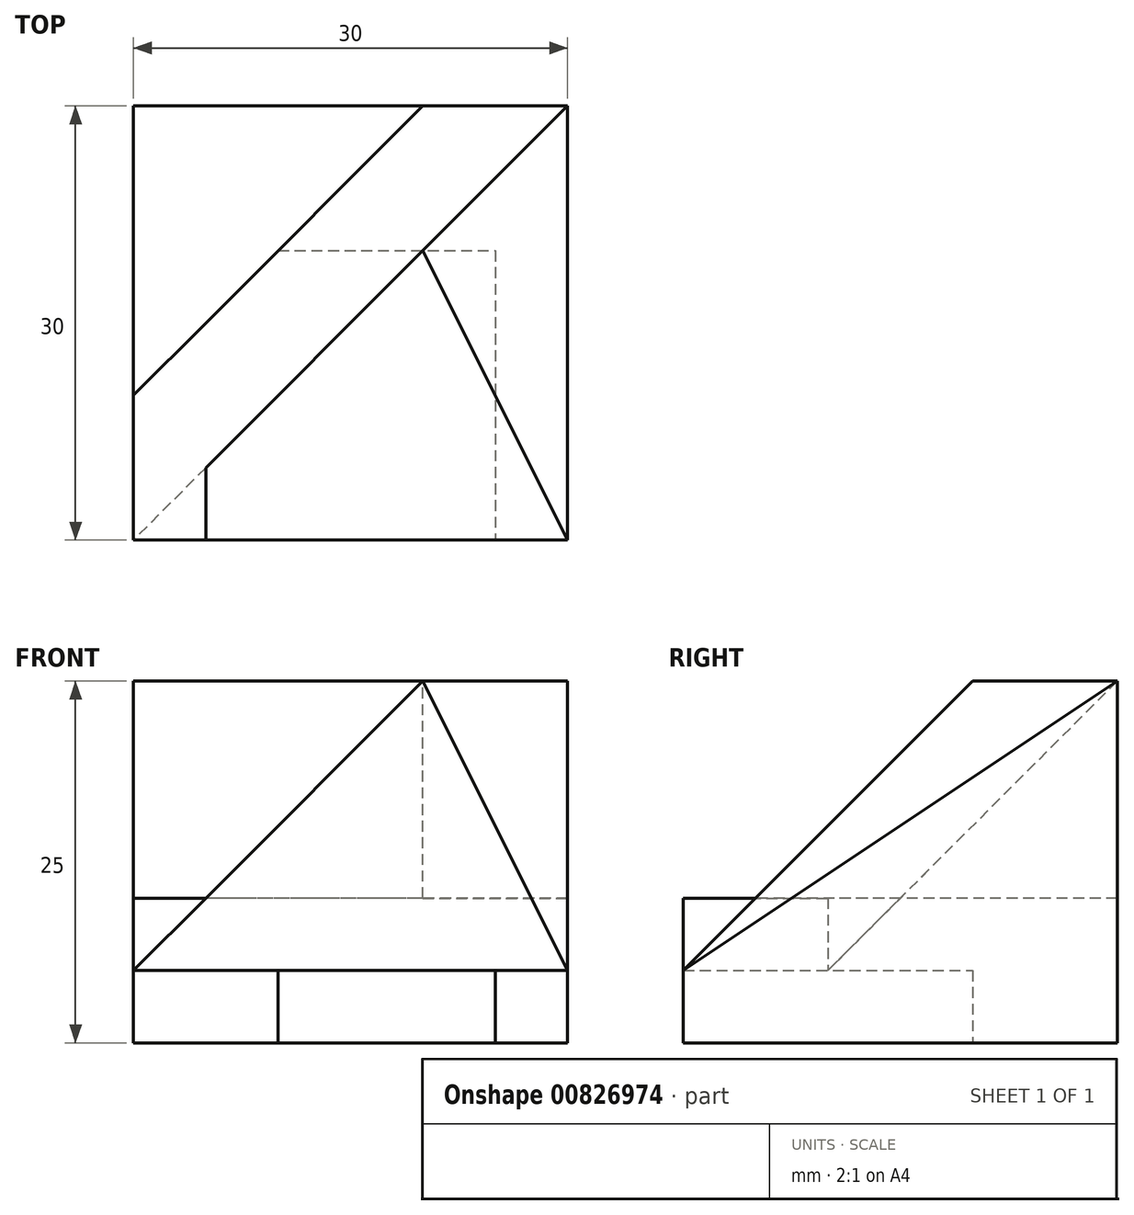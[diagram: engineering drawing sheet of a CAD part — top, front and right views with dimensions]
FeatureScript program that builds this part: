
annotation { "Feature Type Name" : "Feature", "Feature Type Description" : "" }
export const myFeature = defineFeature(function(context is Context, id is Id, definition is map)
    precondition{}
    {
        {
            var Q0;
            Q0=qCreatedBy(makeId("Top.planeOp"),FACE);
            var sketch = newSketch(context, id + "F0", { "sketchPlane" : qUnion([Q0])});
            skLineSegment(sketch, "E0.bottom", {"start": v(0, 0) * mm, "end": v(30, 0) * mm});
            skLineSegment(sketch, "E0.top", {"start": v(0, 30) * mm, "end": v(30, 30) * mm});
            skLineSegment(sketch, "E0.left", {"start": v(0, 0) * mm, "end": v(0, 30) * mm});
            skLineSegment(sketch, "E0.right", {"start": v(30, 0) * mm, "end": v(30, 30) * mm});
            skSolve(sketch);
        }
        {
            var Q0;
            Q0=makeQuery(id+"F0.imprint","IMPRINT",FACE,{"disambiguationData":[TD([[makeQuery(id+"F0.imprint","IMPRINT",EDGE,{"derivedFrom":sQuery(id+"F0.wireOp",EDGE,"E0.bottom")}),1.0]])]});
            extrude(context, id + "F1", {"entities" : qUnion([Q0]), "depth" : 25 * mm, "offsetDistance" : 25 * mm});
        }
        {
            var Q0;
            Q0=makeQuery(id+"F1.opExtrude","CAP_FACE",FACE,{"disambiguationData":[OSD([sQuery(id+"F0.wireOp",EDGE,"E0.bottom"),sQuery(id+"F0.wireOp",EDGE,"E0.top"),sQuery(id+"F0.wireOp",EDGE,"E0.left"),sQuery(id+"F0.wireOp",EDGE,"E0.right")])],"isStart":false});
            var sketch = newSketch(context, id + "F2", { "sketchPlane" : qUnion([Q0])});
            skLineSegment(sketch, "E1", {"start": v(20, 30) * mm, "end": v(0, 10) * mm});
            skLineSegment(sketch, "E2", {"start": v(30, 30) * mm, "end": v(0, 0) * mm});
            skLineSegment(sketch, "E3", {"start": v(30, 0) * mm, "end": v(20, 20) * mm});
            skSolve(sketch);
        }
        {
            var Q0;
            Q0=makeQuery(id+"F1.opExtrude","SWEPT_FACE",FACE,{"disambiguationData":[OSD([sQuery(id+"F0.wireOp",EDGE,"E0.bottom")])]});
            var sketch = newSketch(context, id + "F3", { "sketchPlane" : qUnion([Q0])});
            skLineSegment(sketch, "E4", {"start": v(0, 5) * mm, "end": v(30, 5) * mm});
            skLineSegment(sketch, "E5", {"start": v(0, 5) * mm, "end": v(20, 25) * mm});
            skLineSegment(sketch, "E6", {"start": v(20, 25) * mm, "end": v(30, 5) * mm});
            skLineSegment(sketch, "E7", {"start": v(10, 5) * mm, "end": v(10, 0) * mm});
            skLineSegment(sketch, "E8", {"start": v(25, 5) * mm, "end": v(25, 0) * mm});
            skLineSegment(sketch, "E9", {"start": v(0, 10) * mm, "end": v(5, 10) * mm, "construction": true});
            skSolve(sketch);
        }
        {
            var Q0;
            Q0=makeQuery(id+"F1.opExtrude","SWEPT_FACE",FACE,{"disambiguationData":[OSD([sQuery(id+"F0.wireOp",EDGE,"E0.right")])]});
            var sketch = newSketch(context, id + "F4", { "sketchPlane" : qUnion([Q0])});
            skLineSegment(sketch, "E10", {"start": v(0, 5) * mm, "end": v(30, 25) * mm});
            skLineSegment(sketch, "E11", {"start": v(0, 5) * mm, "end": v(20, 25) * mm});
            skLineSegment(sketch, "E12", {"start": v(20, 25) * mm, "end": v(0, 25) * mm});
            skLineSegment(sketch, "E13", {"start": v(0, 25) * mm, "end": v(0, 5) * mm});
            skSolve(sketch);
        }
        {
            var Q0;
            Q0=makeQuery(id+"F1.opExtrude","SWEPT_FACE",FACE,{"disambiguationData":[OSD([sQuery(id+"F0.wireOp",EDGE,"E0.left")])]});
            var sketch = newSketch(context, id + "F5", { "sketchPlane" : qUnion([Q0])});
            skLineSegment(sketch, "E14", {"start": v(-30, 25) * mm, "end": v(-10, 5) * mm});
            skLineSegment(sketch, "E15", {"start": v(0, 10) * mm, "end": v(-30, 10) * mm});
            skLineSegment(sketch, "E16", {"start": v(-10, 5) * mm, "end": v(-10, 10) * mm});
            skSolve(sketch);
        }
        {
            var Q0;
            Q0=makeQuery(id+"F1.opExtrude","CAP_FACE",FACE,{"disambiguationData":[OSD([sQuery(id+"F0.wireOp",EDGE,"E0.bottom"),sQuery(id+"F0.wireOp",EDGE,"E0.top"),sQuery(id+"F0.wireOp",EDGE,"E0.left"),sQuery(id+"F0.wireOp",EDGE,"E0.right")])],"isStart":true});
            var sketch = newSketch(context, id + "F6", { "sketchPlane" : qUnion([Q0])});
            skLineSegment(sketch, "E17", {"start": v(10, 0) * mm, "end": v(10, -20) * mm});
            skLineSegment(sketch, "E18", {"start": v(10, -20) * mm, "end": v(25, -20) * mm});
            skLineSegment(sketch, "E19", {"start": v(25, -20) * mm, "end": v(25, 0) * mm});
            skSolve(sketch);
        }
        {
            var Q1;
            {var subQ0=sQuery(id+"F2.wireOp",EDGE,"E1");Q1=makeQuery(id+"F2.imprint","IMPRINT",FACE,{"disambiguationData":[TD([[makeQuery(id+"F2.imprint","IMPRINT",EDGE,{"derivedFrom":subQ0}),-1.0]])]});}
            var Q2;
            Q2=sQuery(id+"F5.wireOp",VERTEX,"E14.end");
            loft(context, id + "F7", {"operationType" : NewBodyOperationType.REMOVE, "sheetProfilesArray" : [{ "sheetProfileEntities" : qUnion([Q1]) }, { "sheetProfileEntities" : qUnion([Q2]) }]});
        }
        {
            var Q1;
            {var subQ2=sQuery(id+"F2.wireOp",EDGE,"E3");Q1=makeQuery(id+"F2.imprint","IMPRINT",FACE,{"disambiguationData":[TD([[makeQuery(id+"F2.imprint","IMPRINT",EDGE,{"derivedFrom":subQ2}),-1.0]])]});}
            var Q2;
            Q2=sQuery(id+"F3.wireOp",VERTEX,"E4.end");
            loft(context, id + "F8", {"operationType" : NewBodyOperationType.REMOVE, "sheetProfilesArray" : [{ "sheetProfileEntities" : qUnion([Q1]) }, { "sheetProfileEntities" : qUnion([Q2]) }]});
        }
        {
            var Q1;
            {var subQ0=sQuery(id+"F3.wireOp",EDGE,"E6");Q1=makeQuery(id+"F3.imprint","IMPRINT",FACE,{"disambiguationData":[TD([[makeQuery(id+"F3.imprint","IMPRINT",EDGE,{"derivedFrom":subQ0}),1.0]])]});}
            var Q2;
            Q2=sQuery(id+"F2.wireOp",VERTEX,"E3.end");
            loft(context, id + "F9", {"operationType" : NewBodyOperationType.REMOVE, "sheetProfilesArray" : [{ "sheetProfileEntities" : qUnion([Q1]) }, { "sheetProfileEntities" : qUnion([Q2]) }]});
        }
        {
            var Q0;
            {var subQ0=sQuery(id+"F6.wireOp",EDGE,"E17");Q0=makeQuery(id+"F6.imprint","IMPRINT",FACE,{"disambiguationData":[TD([[makeQuery(id+"F6.imprint","IMPRINT",EDGE,{"derivedFrom":subQ0}),1.0]])]});}
            extrude(context, id + "F10", {"entities" : qUnion([Q0]), "operationType" : NewBodyOperationType.REMOVE, "oppositeDirection" : true, "depth" : 5 * mm, "offsetDistance" : 25 * mm});
        }
        {
            var Q0;
            Q0=makeQuery(id+"F4.imprint","IMPRINT",FACE,{"disambiguationData":[TD([[makeQuery(id+"F4.imprint","IMPRINT",EDGE,{"derivedFrom":sQuery(id+"F4.wireOp",EDGE,"E11")}),1.0]])]});
            extrude(context, id + "F11", {"entities" : qUnion([Q0]), "operationType" : NewBodyOperationType.REMOVE, "endBound" : BoundingType.THROUGH_ALL, "oppositeDirection" : true, "depth" : 25 * mm, "offsetDistance" : 25 * mm});
        }
        {
            var Q0;
            {var subQ3=sQuery(id+"F2.wireOp",EDGE,"E1");Q0=makeQuery(id+"F2.imprint","IMPRINT",FACE,{"disambiguationData":[TD([[makeQuery(id+"F2.imprint","IMPRINT",EDGE,{"derivedFrom":subQ3}),1.0]])]});}
            extrude(context, id + "F12", {"entities" : qUnion([Q0]), "operationType" : NewBodyOperationType.REMOVE, "oppositeDirection" : true, "depth" : 15 * mm, "offsetDistance" : 25 * mm});
        }
        {
            var Q0;
            {var subQ1=sQuery(id+"F0.wireOp",EDGE,"E0.bottom");var subQ2=sQuery(id+"F0.wireOp",EDGE,"E0.left");Q0=makeQuery(id+"F11.boolean.opBoolean","SPLIT",FACE,{"disambiguationData":[TD([makeQuery(id+"F1.opExtrude","SWEPT_FACE",FACE,{"disambiguationData":[OSD([subQ2])]})])],"derivedFrom":makeQuery(id+"F1.opExtrude","SWEPT_FACE",FACE,{"disambiguationData":[OSD([subQ1])]})});}
            var sketch = newSketch(context, id + "F13", { "sketchPlane" : qUnion([Q0])});
            skLineSegment(sketch, "E20", {"start": v(5, 10) * mm, "end": v(0, 5) * mm});
            skLineSegment(sketch, "E21", {"start": v(0, 5) * mm, "end": v(0, 10) * mm});
            skLineSegment(sketch, "E22", {"start": v(0, 10) * mm, "end": v(5, 10) * mm});
            skSolve(sketch);
        }
        {
            var Q0;
            Q0=makeQuery(id+"F13.imprint","IMPRINT",FACE,{"disambiguationData":[TD([[makeQuery(id+"F13.imprint","IMPRINT",EDGE,{"derivedFrom":sQuery(id+"F13.wireOp",EDGE,"E20")}),-1.0]])]});
            extrude(context, id + "F14", {"entities" : qUnion([Q0]), "operationType" : NewBodyOperationType.ADD, "endBound" : BoundingType.UP_TO_NEXT, "oppositeDirection" : true, "depth" : 25 * mm, "offsetDistance" : 25 * mm});
        }
    });
